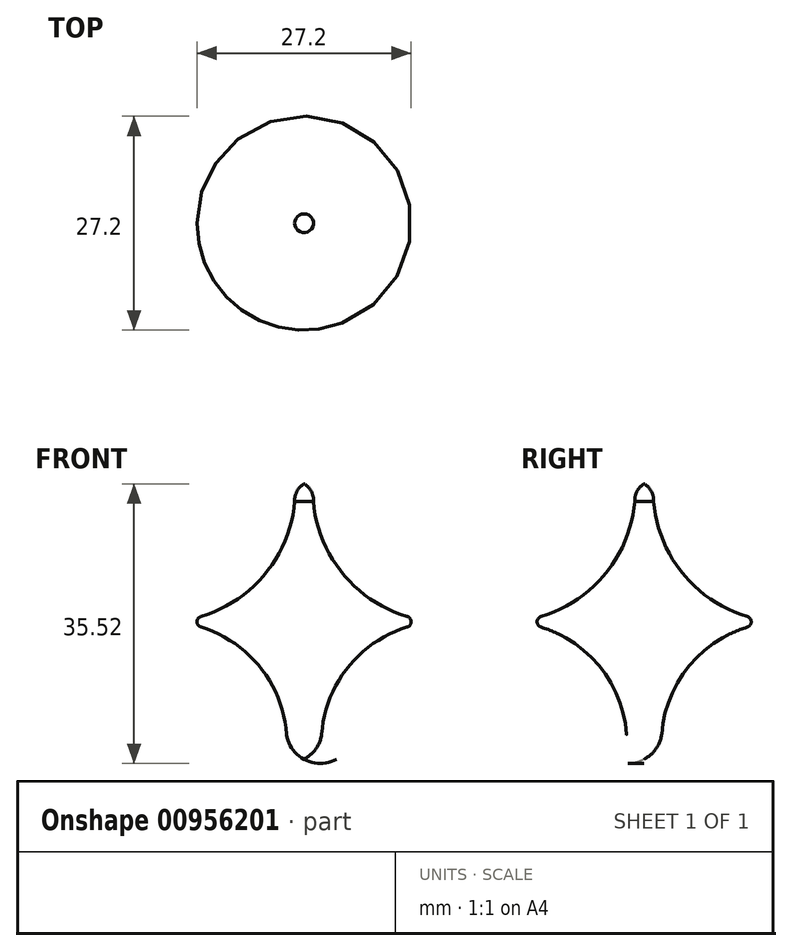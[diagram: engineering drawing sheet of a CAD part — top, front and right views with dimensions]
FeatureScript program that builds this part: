
annotation { "Feature Type Name" : "Feature", "Feature Type Description" : "" }
export const myFeature = defineFeature(function(context is Context, id is Id, definition is map)
    precondition{}
    {
        {
            var Q0;
            Q0=qCreatedBy(makeId("Front.planeOp"),FACE);
            var sketch = newSketch(context, id + "F0", { "sketchPlane" : qUnion([Q0])});
            skLineSegment(sketch, "E0", {"start": v(0, 17.55) * mm, "end": v(0, -17.45) * mm});
            skArc(sketch, "E1", {"start": v(-17.57, 0) * mm, "mid": v(-6.43, 4.51) * mm, "end": v(-1.19, 15.33) * mm});
            skArc(sketch, "E2", {"start": v(0, 17.55) * mm, "mid": v(-0.9, 16.6) * mm, "end": v(-1.19, 15.33) * mm});
            skPoint(sketch, "E3", {"position": v(0, 0) * mm});
            skLineSegment(sketch, "E4", {"start": v(-17.57, 0) * mm, "end": v(0, 0) * mm});
            skArc(sketch, "E5", {"start": v(-2.23, -14.3) * mm, "mid": v(-7.09, -4.13) * mm, "end": v(-17.57, 0) * mm});
            skArc(sketch, "E6", {"start": v(-2.23, -14.3) * mm, "mid": v(-1.49, -16.14) * mm, "end": v(0, -17.45) * mm});
            skSolve(sketch);
        }
        {
            var Q0;
            Q0=qSketchRegion(id+"F0",true);
            var Q1;
            Q1=sQuery(id+"F0.wireOp",EDGE,"E0");
            revolve(context, id + "F1", {"surfaceOperationType" : NewSurfaceOperationType.NEW, "entities" : qUnion([Q0]), "axis" : qUnion([Q1]), "revolveType" : RevolveType.FULL});
        }
        {
            var Q0;
            Q0=makeQuery(id+"F1.opRevolve","SWEPT_FACE",FACE,{"disambiguationData":[OSD([sQuery(id+"F0.wireOp",EDGE,"E5")])]});
            fillet(context, id + "F2", {"entities" : qUnion([Q0]), "radius" : 0.7 * mm, "tangentPropagation" : true, "allowEdgeOverflow" : false});
        }
    });
